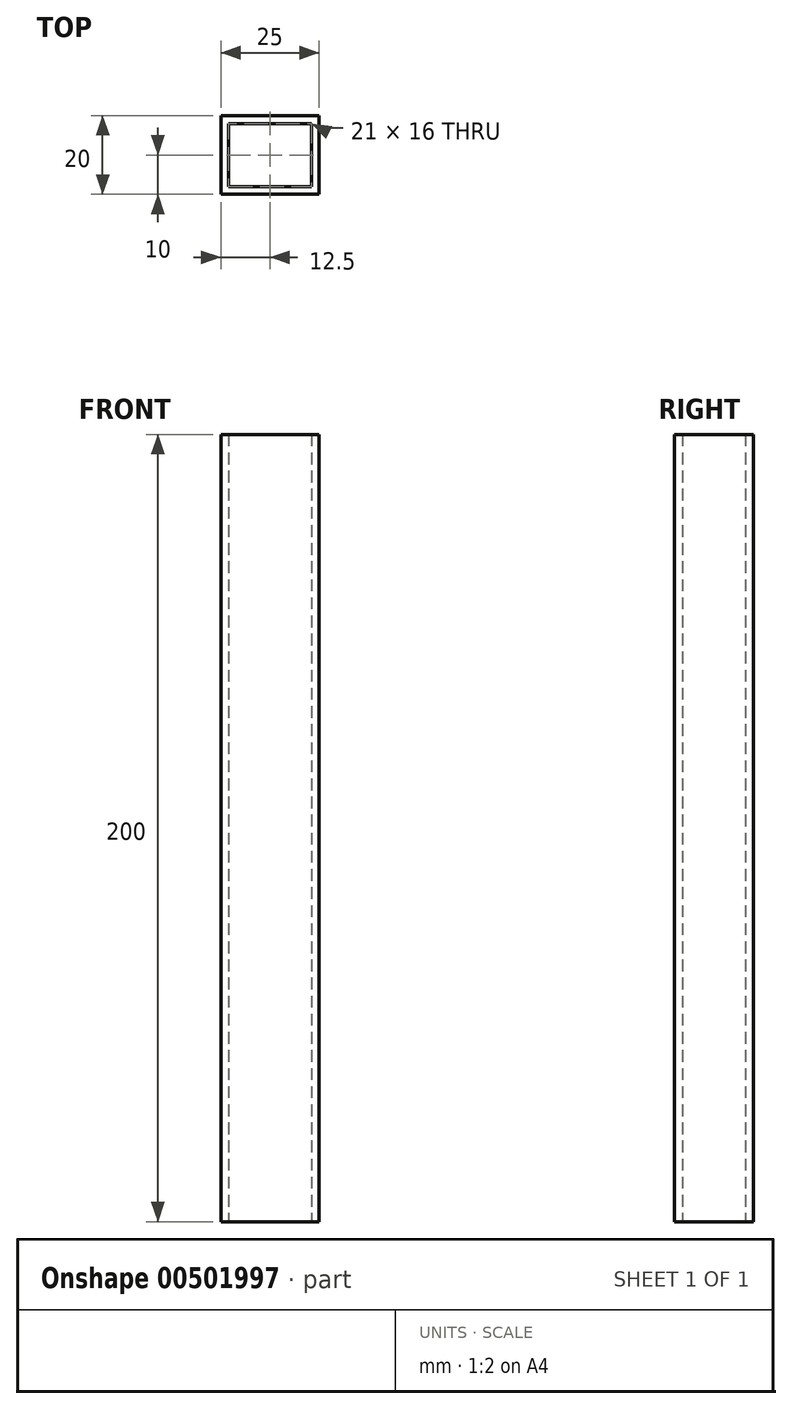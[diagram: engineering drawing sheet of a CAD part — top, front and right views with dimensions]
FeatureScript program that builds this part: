
annotation { "Feature Type Name" : "Feature", "Feature Type Description" : "" }
export const myFeature = defineFeature(function(context is Context, id is Id, definition is map)
    precondition{}
    {
        {
            assignVariable(context, id + "F0", {"name" : "length", "anyValue" : 200 * mm});
        }
        {
            var Q0;
            Q0=qCreatedBy(makeId("Top.planeOp"),FACE);
            var sketch = newSketch(context, id + "F1", { "sketchPlane" : qUnion([Q0])});
            skLineSegment(sketch, "E0.bottom", {"start": v(0, 0) * mm, "end": v(25, 0) * mm});
            skLineSegment(sketch, "E0.top", {"start": v(0, 20) * mm, "end": v(25, 20) * mm});
            skLineSegment(sketch, "E0.left", {"start": v(0, 0) * mm, "end": v(0, 20) * mm});
            skLineSegment(sketch, "E0.right", {"start": v(25, 0) * mm, "end": v(25, 20) * mm});
            skLineSegment(sketch, "E1.bottom", {"start": v(23, 2) * mm, "end": v(2, 2) * mm});
            skLineSegment(sketch, "E1.top", {"start": v(23, 18) * mm, "end": v(2, 18) * mm});
            skLineSegment(sketch, "E1.left", {"start": v(23, 2) * mm, "end": v(23, 18) * mm});
            skLineSegment(sketch, "E1.right", {"start": v(2, 2) * mm, "end": v(2, 18) * mm});
            skPoint(sketch, "E1.middle", {"position": v(12.5, 10) * mm});
            skPoint(sketch, "E1.middle.positionSnap0", {"position": v(0, 10) * mm});
            skPoint(sketch, "E1.middle.positionSnap1", {"position": v(12.5, 20) * mm});
            skPoint(sketch, "E1.centerSnap0", {"position": v(0, 10) * mm});
            skPoint(sketch, "E1.centerSnap1", {"position": v(12.5, 20) * mm});
            skSolve(sketch);
        }
        {
            var Q0;
            Q0 = qSketchRegion(id + "F1", true);
            extrude(context, id + "F2", {"entities" : qUnion([Q0]), "depth" : getVariable(context, 'length')});
        }
    });
